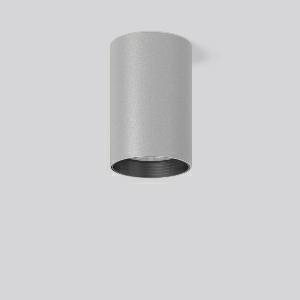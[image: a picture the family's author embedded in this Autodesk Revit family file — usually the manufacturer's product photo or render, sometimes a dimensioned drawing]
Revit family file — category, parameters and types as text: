
# Revit family: heledon_maxi_a_931229_004_1d04
name_source: partatom
category: Lighting Fixtures
units: mm (PartAtom-declared; Revit-internal decimal feet)

## family parameters
Cut with Voids When Loaded = No
Host = Face
Light Source = No
Part Type = Normal
Room Calculation Point = No
Round Connector Dimension = Use Diameter
Shared = No

## types (1)
- HELEDON maxi A (1 x LED Modul 930, 3600 lm, 3000)
    Apparent Load = 35 VA
    Approval mark = CE
    CIE Flux Codes = 96 100 100 100 100
    Color Rendering = 90
    Color Temperature = 3000
    Default Elevation = 1800 mm
    Description = Series: HELEDON maxi
Cylindrical surface-mounted downlight. Housing: die-cast aluminium, powder-coated. Internal ceiling frame polycarbonate with bayonet mounting. Black plastic ring and recessed LED to prevent glare from the side. Optical assembly with lens made of plastic (polycarbonate) for the best homogeneous light distribution - can be changed without tools. Best colour rendering index Ra>90. Suitable for Ceiling mounting. Easy installation with a separate ceiling frame with bayonet mounting and plug connection. Driver integrated. Connected via plug-in connector. High quality converter without flickering and stroboscopic effect. The following accessories can be mounted without use of tools: interchangeable lenses, decorative glasses, honeycomb louvre, clear and frosted diffusers, white interchangeable plastic ring. 
Colour: silver
Diameter: 123 mm
Height: 183 mm
Lamp: LED
Socket: without socket
Colour temperature: 3000K
Colour rendering index (CRI): 92
System power: 35 W
Rated luminous flux: 3600 lm
Luminous efficiency: 103 lm/W
Control gear: Regulated power supply
Protection class: I
Type of protection: IP 20
    Height = 183 mm
    Lamp = 1 x LED Modul 930
    Lamp Light Flux = 3600 lm
    Lamp count = 1
    Length = 123 mm
    Lifetime = 50000 h
    Luminous efficacy = 103 lm/W
    Manufacturer = RZB
    ModVariant = No
    Model = 931229.004
    Mounting Place = Ceiling
    Mounting Type = Surface mounted
    Number of Poles = 1
    OnlyDefault = Yes
    Power Factor = 1
    Product Name = HELEDON maxi A
    Product group = Surface mounted downlights
    ProductGroupID = 302
    Protection Class = Protection class I
    Protection Degree = IP 20
    RLX_Detail_Level = 1
    RLX_Emergency_Light_Flux = 0 lm
    RLX_Emergency_Type = 0
    RLX_Emergency_Type_DB = No
    RlxData = <blob elided: 100305 chars, md5=f0ebe87f>
    Socket = socket
    Standby Power = 0 W
    System Light Flux = 3600 lm
    System Power = 35 W
    Type Comments = Product without accessories
    Type Image = 931193.004.jpg
    URL = http://relux.com
    VarID = ---
    Voltage = 230 V
    Voltage Range = 220-240 V
    Weight = 0.00 kg
    Width = 0 mm  [stored 0 ft]

note: [stored X ft] marks values corroborated as IEEE doubles in the binary element streams (Revit-internal decimal feet)

## geometry (parser evidence)
native form markers: Blend x4, Sweep x10
no freeform markers — native parametric forms only
